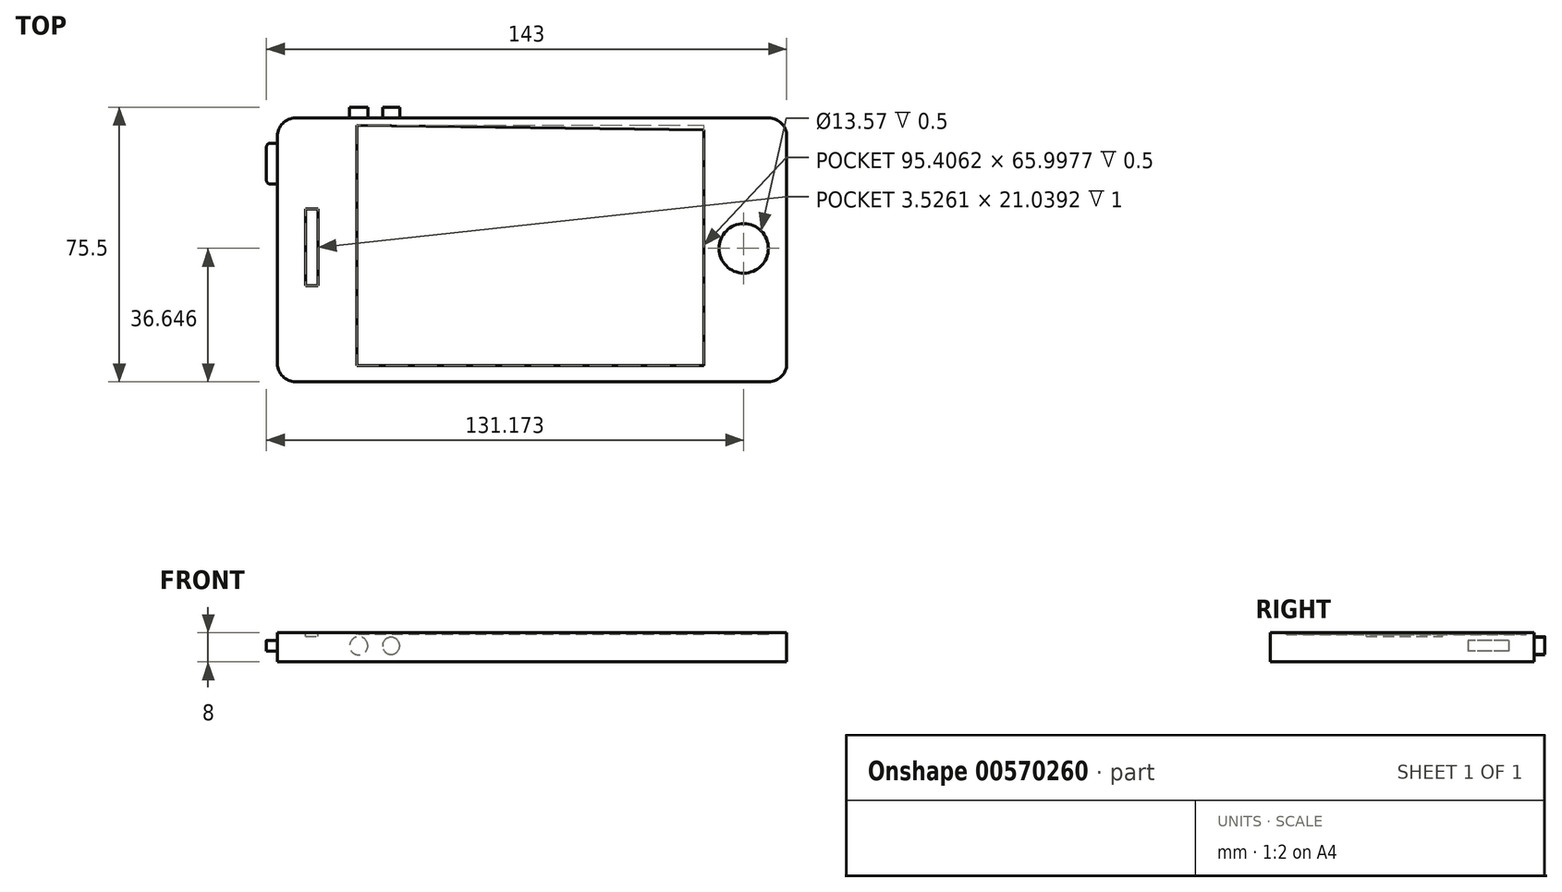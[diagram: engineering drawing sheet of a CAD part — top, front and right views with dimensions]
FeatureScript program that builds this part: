
annotation { "Feature Type Name" : "Feature", "Feature Type Description" : "" }
export const myFeature = defineFeature(function(context is Context, id is Id, definition is map)
    precondition{}
    {
        {
            var Q0;
            Q0=qCreatedBy(makeId("Top.planeOp"),FACE);
            var sketch = newSketch(context, id + "F0", { "sketchPlane" : qUnion([Q0])});
            skLineSegment(sketch, "E0.bottom", {"start": v(72.47, 46.08) * mm, "end": v(-67.53, 46.08) * mm});
            skLineSegment(sketch, "E0.top", {"start": v(72.47, -26.42) * mm, "end": v(-67.53, -26.42) * mm});
            skLineSegment(sketch, "E0.left", {"start": v(72.47, 46.08) * mm, "end": v(72.47, -26.42) * mm});
            skLineSegment(sketch, "E0.right", {"start": v(-67.53, 46.08) * mm, "end": v(-67.53, -26.42) * mm});
            skSolve(sketch);
        }
        {
            var Q0;
            Q0=makeQuery(id+"F0.imprint","IMPRINT",FACE,{"disambiguationData":[TD([[makeQuery(id+"F0.imprint","IMPRINT",EDGE,{"derivedFrom":sQuery(id+"F0.wireOp",EDGE,"E0.bottom")}),1.0]])]});
            extrude(context, id + "F1", {"entities" : qUnion([Q0]), "depth" : 8 * mm, "offsetDistance" : 25 * mm});
        }
        {
            var Q0;
            Q0=makeQuery(id+"F1.opExtrude","SWEPT_EDGE",EDGE,{"disambiguationData":[OSD([sQuery(id+"F0.wireOp",EDGE,"E0.top"),sQuery(id+"F0.wireOp",EDGE,"E0.left")])]});
            var Q1;
            Q1=makeQuery(id+"F1.opExtrude","SWEPT_EDGE",EDGE,{"disambiguationData":[OSD([sQuery(id+"F0.wireOp",EDGE,"E0.bottom"),sQuery(id+"F0.wireOp",EDGE,"E0.left")])]});
            var Q2;
            Q2=makeQuery(id+"F1.opExtrude","SWEPT_EDGE",EDGE,{"disambiguationData":[OSD([sQuery(id+"F0.wireOp",EDGE,"E0.top"),sQuery(id+"F0.wireOp",EDGE,"E0.right")])]});
            var Q3;
            Q3=makeQuery(id+"F1.opExtrude","SWEPT_EDGE",EDGE,{"disambiguationData":[OSD([sQuery(id+"F0.wireOp",EDGE,"E0.bottom"),sQuery(id+"F0.wireOp",EDGE,"E0.right")])]});
            fillet(context, id + "F2", {"entities" : qUnion([Q0, Q1, Q2, Q3]), "radius" : 5 * mm, "tangentPropagation" : true, "allowEdgeOverflow" : false});
        }
        {
            var Q0;
            Q0=makeQuery(id+"F1.opExtrude","CAP_FACE",FACE,{"disambiguationData":[OSD([sQuery(id+"F0.wireOp",EDGE,"E0.bottom"),sQuery(id+"F0.wireOp",EDGE,"E0.top"),sQuery(id+"F0.wireOp",EDGE,"E0.left"),sQuery(id+"F0.wireOp",EDGE,"E0.right")])],"isStart":false});
            var sketch = newSketch(context, id + "F3", { "sketchPlane" : qUnion([Q0])});
            skSolve(sketch);
        }
        {
            var Q0;
            {var subQ3=sQuery(id+"F0.wireOp",EDGE,"E0.bottom");Q0=makeQuery(id+"F3.imprint","IMPRINT",FACE,{"disambiguationData":[TD([[makeQuery(id+"F3.imprint","IMPRINT",EDGE,{"derivedFrom":makeQuery(id+"F1.opExtrude","CAP_EDGE",EDGE,{"disambiguationData":[OSD([subQ3])],"isStart":false})}),1.0]])]});}
            var sketch = newSketch(context, id + "F4", { "sketchPlane" : qUnion([Q0])});
            skLineSegment(sketch, "E1", {"start": v(48.95, 45.76) * mm, "end": v(48.95, -25.46) * mm});
            skCircle(sketch, "E2", {"center": v(60.64, 10.23) * mm, "radius": 6.78 * mm});
            skLineSegment(sketch, "E3", {"start": v(-48.9, 46.2) * mm, "end": v(-48.9, -26.45) * mm});
            skLineSegment(sketch, "E4", {"start": v(-47.02, -24.57) * mm, "end": v(45.6, -24.57) * mm});
            skLineSegment(sketch, "E5", {"start": v(45.6, -24.57) * mm, "end": v(45.6, 43.6) * mm});
            skLineSegment(sketch, "E6", {"start": v(45.6, 43.6) * mm, "end": v(-46.55, 43.6) * mm});
            skLineSegment(sketch, "E7", {"start": v(-47.02, -24.57) * mm, "end": v(-47.02, 43.6) * mm});
            skLineSegment(sketch, "E8", {"start": v(-47.02, 43.6) * mm, "end": v(-44.73, 43.6) * mm});
            skSolve(sketch);
        }
        {
            var Q0;
            Q0=makeQuery(id+"F4.imprint","IMPRINT",FACE,{"disambiguationData":[TD([[makeQuery(id+"F4.imprint","IMPRINT",EDGE,{"derivedFrom":sQuery(id+"F4.wireOp",EDGE,"E2")}),1.0]])]});
            extrude(context, id + "F5", {"entities" : qUnion([Q0]), "operationType" : NewBodyOperationType.ADD, "depth" : 0.5 * mm, "offsetDistance" : 25 * mm});
        }
        {
            var Q0;
            {var subQ3=sQuery(id+"F0.wireOp",EDGE,"E0.bottom");Q0=makeQuery(id+"F3.imprint","IMPRINT",FACE,{"disambiguationData":[TD([[makeQuery(id+"F3.imprint","IMPRINT",EDGE,{"derivedFrom":makeQuery(id+"F1.opExtrude","CAP_EDGE",EDGE,{"disambiguationData":[OSD([subQ3])],"isStart":false})}),1.0]])]});}
            var sketch = newSketch(context, id + "F6", { "sketchPlane" : qUnion([Q0])});
            skLineSegment(sketch, "E9", {"start": v(-45.7, 44.03) * mm, "end": v(-45.7, -21.97) * mm});
            skLineSegment(sketch, "E10", {"start": v(-45.7, -21.97) * mm, "end": v(49.7, -21.97) * mm});
            skLineSegment(sketch, "E11", {"start": v(49.7, -21.97) * mm, "end": v(49.7, 42.79) * mm});
            skLineSegment(sketch, "E12", {"start": v(49.7, 42.79) * mm, "end": v(-45.7, 44.03) * mm});
            skLineSegment(sketch, "E13", {"start": v(-60.27, 21) * mm, "end": v(-60.27, 5.2) * mm});
            skLineSegment(sketch, "E14", {"start": v(-60.27, 5.2) * mm, "end": v(-56.5, 5.16) * mm});
            skLineSegment(sketch, "E15", {"start": v(-56.5, 5.16) * mm, "end": v(-56.5, 21) * mm});
            skLineSegment(sketch, "E16", {"start": v(-56.5, 21) * mm, "end": v(-60.27, 21) * mm});
            skSolve(sketch);
        }
        {
            var Q0;
            Q0=makeQuery(id+"F6.imprint","IMPRINT",FACE,{"disambiguationData":[TD([[makeQuery(id+"F6.imprint","IMPRINT",EDGE,{"derivedFrom":sQuery(id+"F6.wireOp",EDGE,"E9")}),1.0]])]});
            extrude(context, id + "F7", {"entities" : qUnion([Q0]), "operationType" : NewBodyOperationType.REMOVE, "oppositeDirection" : true, "depth" : 0.5 * mm, "offsetDistance" : 25 * mm});
        }
        {
            var Q0;
            Q0=makeQuery(id+"F5.opExtrude","CAP_FACE",FACE,{"disambiguationData":[OSD([sQuery(id+"F4.wireOp",EDGE,"E2")])],"isStart":false});
            extrude(context, id + "F8", {"entities" : qUnion([Q0]), "operationType" : NewBodyOperationType.REMOVE, "oppositeDirection" : true, "depth" : 1 * mm, "offsetDistance" : 25 * mm});
        }
        {
            var Q0;
            {var subQ3=sQuery(id+"F0.wireOp",EDGE,"E0.bottom");Q0=makeQuery(id+"F3.imprint","IMPRINT",FACE,{"disambiguationData":[TD([[makeQuery(id+"F3.imprint","IMPRINT",EDGE,{"derivedFrom":makeQuery(id+"F1.opExtrude","CAP_EDGE",EDGE,{"disambiguationData":[OSD([subQ3])],"isStart":false})}),1.0]])]});}
            var sketch = newSketch(context, id + "F9", { "sketchPlane" : qUnion([Q0])});
            skLineSegment(sketch, "E17.bottom", {"start": v(-59.83, 0) * mm, "end": v(-56.3, 0) * mm});
            skLineSegment(sketch, "E17.top", {"start": v(-59.83, 21.04) * mm, "end": v(-56.3, 21.04) * mm});
            skLineSegment(sketch, "E17.left", {"start": v(-59.83, 0) * mm, "end": v(-59.83, 21.04) * mm});
            skLineSegment(sketch, "E17.right", {"start": v(-56.3, 0) * mm, "end": v(-56.3, 21.04) * mm});
            skSolve(sketch);
        }
        {
            var Q0;
            Q0=makeQuery(id+"F9.imprint","IMPRINT",FACE,{"disambiguationData":[TD([[makeQuery(id+"F9.imprint","IMPRINT",EDGE,{"derivedFrom":sQuery(id+"F9.wireOp",EDGE,"E17.bottom")}),1.0]])]});
            extrude(context, id + "F10", {"entities" : qUnion([Q0]), "operationType" : NewBodyOperationType.REMOVE, "oppositeDirection" : true, "depth" : 1 * mm, "offsetDistance" : 25 * mm});
        }
        {
            var Q0;
            Q0=makeQuery(id+"F1.opExtrude","SWEPT_FACE",FACE,{"disambiguationData":[OSD([sQuery(id+"F0.wireOp",EDGE,"E0.right")])]});
            var sketch = newSketch(context, id + "F11", { "sketchPlane" : qUnion([Q0])});
            skLineSegment(sketch, "E18.bottom", {"start": v(-39.15, 5.9) * mm, "end": v(-27.94, 5.9) * mm});
            skLineSegment(sketch, "E18.top", {"start": v(-39.15, 2.93) * mm, "end": v(-27.94, 2.93) * mm});
            skLineSegment(sketch, "E18.left", {"start": v(-39.15, 5.9) * mm, "end": v(-39.15, 2.93) * mm});
            skLineSegment(sketch, "E18.right", {"start": v(-27.94, 5.9) * mm, "end": v(-27.94, 2.93) * mm});
            skSolve(sketch);
        }
        {
            var Q0;
            Q0=makeQuery(id+"F11.imprint","IMPRINT",FACE,{"disambiguationData":[TD([[makeQuery(id+"F11.imprint","IMPRINT",EDGE,{"derivedFrom":sQuery(id+"F11.wireOp",EDGE,"E18.bottom")}),-1.0]])]});
            extrude(context, id + "F12", {"entities" : qUnion([Q0]), "operationType" : NewBodyOperationType.ADD, "depth" : 3 * mm, "offsetDistance" : 25 * mm});
        }
        {
            var Q0;
            Q0=makeQuery(id+"F12.opExtrude","CAP_EDGE",EDGE,{"disambiguationData":[OSD([sQuery(id+"F11.wireOp",EDGE,"E18.right")])],"isStart":false});
            var Q1;
            Q1=makeQuery(id+"F12.opExtrude","CAP_EDGE",EDGE,{"disambiguationData":[OSD([sQuery(id+"F11.wireOp",EDGE,"E18.left")])],"isStart":false});
            fillet(context, id + "F13", {"entities" : qUnion([Q0, Q1]), "radius" : 1 * mm, "tangentPropagation" : true, "allowEdgeOverflow" : false});
        }
        {
            var Q0;
            Q0=makeQuery(id+"F1.opExtrude","SWEPT_FACE",FACE,{"disambiguationData":[OSD([sQuery(id+"F0.wireOp",EDGE,"E0.bottom")])]});
            var sketch = newSketch(context, id + "F14", { "sketchPlane" : qUnion([Q0])});
            skCircle(sketch, "E19", {"center": v(45.18, 4.4) * mm, "radius": 2.5 * mm});
            skCircle(sketch, "E20", {"center": v(36.28, 4.4) * mm, "radius": 2.35 * mm});
            skSolve(sketch);
        }
        {
            var Q0;
            Q0=makeQuery(id+"F14.imprint","IMPRINT",FACE,{"disambiguationData":[TD([[makeQuery(id+"F14.imprint","IMPRINT",EDGE,{"derivedFrom":sQuery(id+"F14.wireOp",EDGE,"E19")}),1.0]])]});
            var Q1;
            Q1=makeQuery(id+"F14.imprint","IMPRINT",FACE,{"disambiguationData":[TD([[makeQuery(id+"F14.imprint","IMPRINT",EDGE,{"derivedFrom":sQuery(id+"F14.wireOp",EDGE,"E20")}),1.0]])]});
            extrude(context, id + "F15", {"entities" : qUnion([Q0, Q1]), "operationType" : NewBodyOperationType.ADD, "depth" : 3 * mm, "offsetDistance" : 25 * mm});
        }
    });
